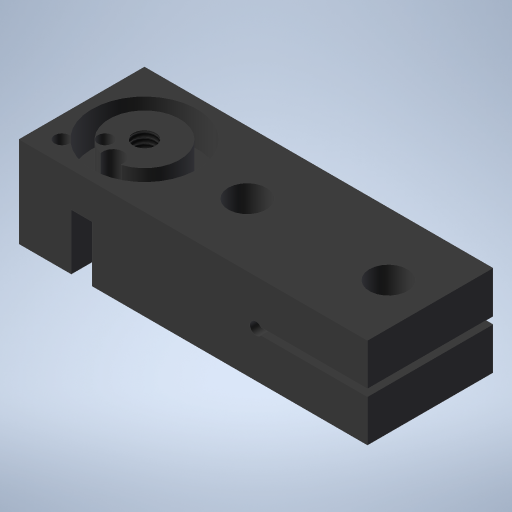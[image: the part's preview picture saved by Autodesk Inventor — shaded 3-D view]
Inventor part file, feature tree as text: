
AUTODESK INVENTOR PART (.ipt)
format: ipt  version: 2024 (Build 280153000, 153)  size: 303,616 bytes
history: native  units: in
note: dims shown in document units (in); Inventor stores cm internally (conversion verified against a paired STEP export)
features: extrude x3, sketch x3, hole x3
ambient origin geometry x8: Origin, YZ Plane, XZ Plane, XY Plane, X Axis, Y Axis, Z Axis, Center Point
bodies: Solid1 (feature_tree)
feature tree (9):
  extrude  "Extrusion1"  Depth=0.5118in
  sketch  "Sketch2"  dims[d2=0.6299in d3=0.0701in]
  hole  "Hole1"  [1 undecoded]
  extrude  "Extrusion2"  Depth=0.3346in
  sketch  "Sketch3"  dims[d4=0.0197in d5=0.0197in d6=0.7087in d7=0.0in d8=0.2362in d9=0.7972in d10=0.3445in d11=0.3445in d12=0.2953in d13=0.0591in d14=0.1969in d15=0.1181in d16=0.2165in d17=0.1575in d18=0.3937in d19=0.2244in d20=90.0deg d21=0.315in d22=0.8108in d23=0.315in d24=0.0in d25=45.0deg d26=0.5945in d27=0.3976in d28=0.1575in d29=0.0984in d30=0.1181in d31=0.0421in d32=0.0854in d33=0.1718in d34=0.0854in d35=0.1969in d36=0.0in d37=0.1276in d38=0.315in d39=0.1575in d40=0.0787in d41=90.0deg d42=0.3346in d43=0.8108in d44=0.0854in d45=0.315in d46=0.1575in d47=0.0787in d48=90.0deg d49=0.3346in d50=0.0in]
  extrude  "Extrusion3"  Depth=0.7087in TaperAngle=0.0deg
  hole  "Hole2"  [1 undecoded]
  hole  "Hole3"  [1 undecoded]
  sketch  "Sketch1"  dims[d0=1.9685in d1=0.5118in]
note: 3 required parameter values undecoded (feature->parameter linkage not recoverable at this tier; creation-order binding heuristic only, values carry confidence <= 0.55)
